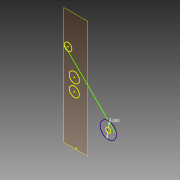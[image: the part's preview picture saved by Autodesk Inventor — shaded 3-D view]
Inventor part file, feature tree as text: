
AUTODESK INVENTOR PART (.ipt)
format: ipt  version: 2013 (Build 170138000, 138)  size: 61,952 bytes
history: native  units: in
note: dims shown in document units (in); Inventor stores cm internally (conversion verified against a paired STEP export)
features: reference x4, plane x1, sketch x1
ambient origin geometry x8: Origin, YZ Plane, XZ Plane, XY Plane, X Axis, Y Axis, Z Axis, Center Point
feature tree (6):
  plane  "Work Plane1"
  sketch  "Sketch1"  dims[d0=4.0in]
  reference  "Reference1"
  reference  "Reference2"
  reference  "Reference3"
  reference  "Reference4"
